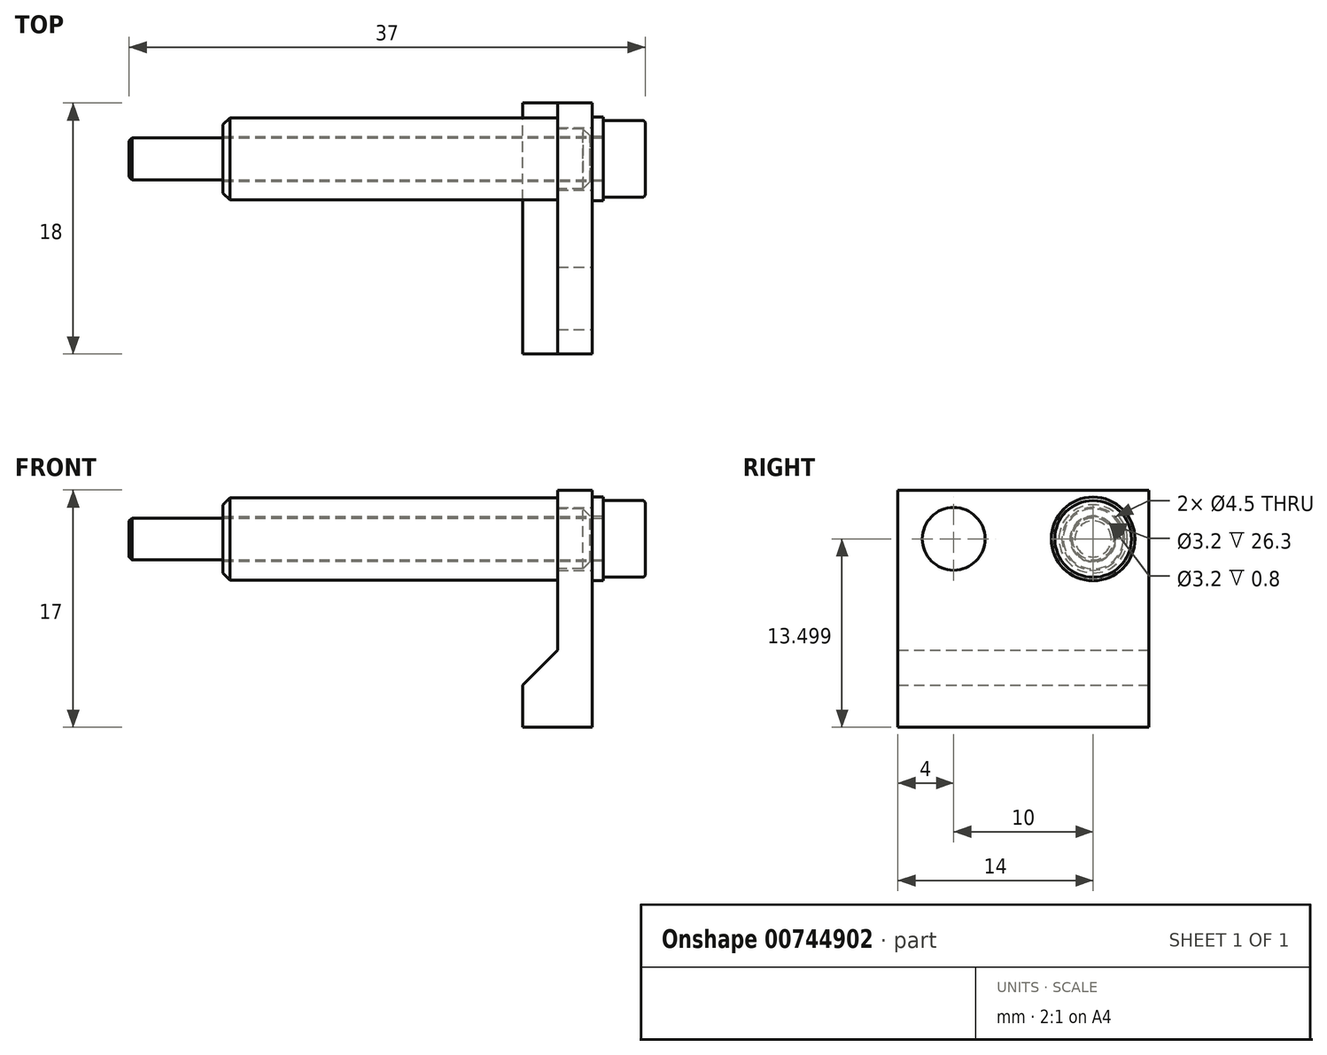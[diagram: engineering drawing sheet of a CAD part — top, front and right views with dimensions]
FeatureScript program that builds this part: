
annotation { "Feature Type Name" : "Feature", "Feature Type Description" : "" }
export const myFeature = defineFeature(function(context is Context, id is Id, definition is map)
    precondition{}
    {
        {
            var Q0;
            Q0=qCreatedBy(makeId("Front.planeOp"),FACE);
            var sketch = newSketch(context, id + "F0", { "sketchPlane" : qUnion([Q0])});
            skLineSegment(sketch, "E0", {"start": v(7.36, -9.32) * mm, "end": v(7.36, -5.59) * mm, "construction": true});
            skLineSegment(sketch, "E1", {"start": v(7.36, -5.59) * mm, "end": v(8.08, -5.59) * mm, "construction": true});
            skLineSegment(sketch, "E2", {"start": v(7.36, -9.32) * mm, "end": v(0, -9.32) * mm, "construction": true});
            skLineSegment(sketch, "E3", {"start": v(8.08, 0) * mm, "end": v(0, 0) * mm, "construction": true});
            skLineSegment(sketch, "E4", {"start": v(10.6, -3.06) * mm, "end": v(10.6, -2.53) * mm, "construction": true});
            skLineSegment(sketch, "E5", {"start": v(8.08, -5.59) * mm, "end": v(8.78, -4.88) * mm, "construction": true});
            skLineSegment(sketch, "E6", {"start": v(10.6, -2.53) * mm, "end": v(8.08, 0) * mm, "construction": true});
            skLineSegment(sketch, "E7", {"start": v(8.08, 0) * mm, "end": v(8.08, -5.59) * mm, "construction": true});
            skLineSegment(sketch, "E8", {"start": v(9.5, -4.17) * mm, "end": v(0, -4.17) * mm, "construction": true});
            skLineSegment(sketch, "E9", {"start": v(9.5, -4.17) * mm, "end": v(9.5, -1.42) * mm, "construction": true});
            skLineSegment(sketch, "E10", {"start": v(9.5, -1.42) * mm, "end": v(0, -1.42) * mm, "construction": true});
            skLineSegment(sketch, "E11", {"start": v(0, 0) * mm, "end": v(0, -1.42) * mm, "construction": true});
            skLineSegment(sketch, "E12", {"start": v(0, -4.17) * mm, "end": v(0, -9.32) * mm, "construction": true});
            skLineSegment(sketch, "E13", {"start": v(0, -4.17) * mm, "end": v(0, -1.42) * mm, "construction": true});
            skLineSegment(sketch, "E14.MirrorCS", {"start": v(-7.36, -5.59) * mm, "end": v(-8.08, -5.59) * mm, "construction": true});
            skLineSegment(sketch, "E15.MirrorCS", {"start": v(-8.08, -5.59) * mm, "end": v(-10.6, -3.06) * mm, "construction": true});
            skLineSegment(sketch, "E16.MirrorCS", {"start": v(-10.6, -3.06) * mm, "end": v(-10.6, -2.53) * mm, "construction": true});
            skLineSegment(sketch, "E17.MirrorCS", {"start": v(-10.6, -2.53) * mm, "end": v(-8.08, 0) * mm, "construction": true});
            skLineSegment(sketch, "E18.MirrorCS", {"start": v(-9.5, -1.42) * mm, "end": v(0, -1.42) * mm, "construction": true});
            skLineSegment(sketch, "E19.MirrorCS", {"start": v(-8.08, 0) * mm, "end": v(0, 0) * mm, "construction": true});
            skLineSegment(sketch, "E20.MirrorCS", {"start": v(-7.36, -9.32) * mm, "end": v(-7.36, -5.59) * mm, "construction": true});
            skLineSegment(sketch, "E21.MirrorCS", {"start": v(-9.5, -4.17) * mm, "end": v(-9.5, -1.42) * mm, "construction": true});
            skLineSegment(sketch, "E22.MirrorCS", {"start": v(-7.36, -9.32) * mm, "end": v(0, -9.32) * mm, "construction": true});
            skLineSegment(sketch, "E23.MirrorCS", {"start": v(-9.5, -4.17) * mm, "end": v(0, -4.17) * mm, "construction": true});
            skLineSegment(sketch, "E24.MirrorCS", {"start": v(-8.08, 0) * mm, "end": v(-8.08, -5.59) * mm, "construction": true});
            skLineSegment(sketch, "E25", {"start": v(8.78, -4.88) * mm, "end": v(10.6, -3.06) * mm});
            skLineSegment(sketch, "E26", {"start": v(10.6, -3.06) * mm, "end": v(11.31, -2.35) * mm});
            skLineSegment(sketch, "E27", {"start": v(8.78, -4.88) * mm, "end": v(8.78, -7.88) * mm});
            skLineSegment(sketch, "E28", {"start": v(8.78, -7.88) * mm, "end": v(13.78, -7.88) * mm});
            skLineSegment(sketch, "E29", {"start": v(13.78, -7.88) * mm, "end": v(13.78, 9.12) * mm});
            skLineSegment(sketch, "E30", {"start": v(11.31, 9.12) * mm, "end": v(11.31, -2.35) * mm});
            skLineSegment(sketch, "E31", {"start": v(13.78, 9.12) * mm, "end": v(11.31, 9.12) * mm});
            skSolve(sketch);
        }
        {
            var Q0;
            Q0 = qSketchRegion(id + "F0", true);
            extrude(context, id + "F1", {"entities" : qUnion([Q0]), "endBound" : BoundingType.SYMMETRIC, "depth" : 18 * mm, "offsetDistance" : 25 * mm});
        }
        {
            var Q0;
            Q0=makeQuery(id+"F1.opExtrude","SWEPT_FACE",FACE,{"disambiguationData":[OSD([sQuery(id+"F0.wireOp",EDGE,"E29")])]});
            var sketch = newSketch(context, id + "F2", { "sketchPlane" : qUnion([Q0])});
            skLineSegment(sketch, "E32", {"start": v(-9, 5.62) * mm, "end": v(-5, 5.62) * mm, "construction": true});
            skLineSegment(sketch, "E33", {"start": v(-5, 5.62) * mm, "end": v(5, 5.62) * mm, "construction": true});
            skLineSegment(sketch, "E34", {"start": v(5, 5.62) * mm, "end": v(9, 5.62) * mm, "construction": true});
            skSolve(sketch);
        }
        {
            var Q0;
            Q0=sQuery(id+"F2.wireOp",VERTEX,"E33.start");
            var Q1;
            Q1=sQuery(id+"F2.wireOp",VERTEX,"E34.start");
            var Q2;
            Q2=makeQuery(id+"F1.opExtrude","SWEPT_BODY",BODY,{"disambiguationData":[OSD([sQuery(id+"F0.wireOp",EDGE,"E25"),sQuery(id+"F0.wireOp",EDGE,"E26"),sQuery(id+"F0.wireOp",EDGE,"E27"),sQuery(id+"F0.wireOp",EDGE,"E28"),sQuery(id+"F0.wireOp",EDGE,"E29"),sQuery(id+"F0.wireOp",EDGE,"jxwox8Iy-gYFC-VK8o-ptvJ-4F3VnWy338mb"),sQuery(id+"F0.wireOp",EDGE,"mAjDmbwP-u3rq-lV9H-9kcG-bIBsuvSuJTE3"),sQuery(id+"F0.wireOp",EDGE,"juroiCpw-intV-WaKl-nkkL-CXtJp0xfCT75"),sQuery(id+"F0.wireOp",EDGE,"E30")])]});
            hole(context, id + "F3", {"style" : HoleStyle.SIMPLE, "endStyle" : HoleEndStyle.THROUGH, "holeDiameter" : 4.5 * mm, "majorDiameter" : 5 * mm, "isTappedThrough" : true, "tappedDepth" : 6 * mm, "tapClearance" : 3, "startFromSketch" : true, "locations" : qUnion([Q0, Q1]), "scope" : qUnion([Q2])});
        }
        {
            var Q0;
            Q0=makeQuery(id+"F1.opExtrude","SWEPT_FACE",FACE,{"disambiguationData":[OSD([sQuery(id+"F0.wireOp",EDGE,"E30")])]});
            var sketch = newSketch(context, id + "F4", { "sketchPlane" : qUnion([Q0])});
            skCircle(sketch, "E35", {"center": v(-5, 5.62) * mm, "radius": 2.95 * mm});
            skSolve(sketch);
        }
        {
            var Q0;
            Q0 = qSketchRegion(id + "F4", true);
            extrude(context, id + "F5", {"entities" : qUnion([Q0]), "depth" : 24 * mm, "offsetDistance" : 25 * mm});
        }
        {
            var Q0;
            Q0=makeQuery(id+"F5.opExtrude","CAP_FACE",FACE,{"disambiguationData":[OSD([sQuery(id+"F4.wireOp",EDGE,"E35")])],"isStart":true});
            var sketch = newSketch(context, id + "F6", { "sketchPlane" : qUnion([Q0])});
            skCircle(sketch, "E36", {"center": v(5, 5.62) * mm, "radius": 2.15 * mm});
            skSolve(sketch);
        }
        {
            var Q0;
            Q0 = qSketchRegion(id + "F6", true);
            extrude(context, id + "F7", {"entities" : qUnion([Q0]), "operationType" : NewBodyOperationType.ADD, "depth" : 2.3 * mm, "offsetDistance" : 25 * mm});
        }
        {
            var Q0;
            Q0=makeQuery(id+"F7.opExtrude","CAP_EDGE",EDGE,{"disambiguationData":[OSD([sQuery(id+"F6.wireOp",EDGE,"E36")])],"isStart":false});
            chamfer(context, id + "F8", {"entities" : qUnion([Q0]), "width" : 0.5 * mm, "tangentPropagation" : true});
        }
        {
            var Q0;
            Q0=makeQuery(id+"F5.opExtrude","CAP_EDGE",EDGE,{"disambiguationData":[OSD([sQuery(id+"F4.wireOp",EDGE,"E35")])],"isStart":false});
            chamfer(context, id + "F9", {"entities" : qUnion([Q0]), "width" : 0.5 * mm, "tangentPropagation" : true});
        }
        {
            var Q0;
            Q0=makeQuery(id+"F7.opExtrude","CAP_FACE",FACE,{"disambiguationData":[OSD([sQuery(id+"F6.wireOp",EDGE,"E36")])],"isStart":false});
            var sketch = newSketch(context, id + "F10", { "sketchPlane" : qUnion([Q0])});
            skPoint(sketch, "E37", {"position": v(5, 5.62) * mm});
            skSolve(sketch);
        }
        {
            var Q0;
            Q0=sQuery(id+"F10.wireOp",VERTEX,"E37");
            var Q1;
            Q1=makeQuery(id+"F5.opExtrude","SWEPT_BODY",BODY,{"disambiguationData":[OSD([sQuery(id+"F4.wireOp",EDGE,"E35")])]});
            hole(context, id + "F11", {"style" : HoleStyle.SIMPLE, "endStyle" : HoleEndStyle.THROUGH, "holeDiameter" : 3.2 * mm, "majorDiameter" : 5 * mm, "isTappedThrough" : true, "tappedDepth" : 6 * mm, "tapClearance" : 3, "startFromSketch" : true, "locations" : qUnion([Q0]), "scope" : qUnion([Q1])});
        }
        {
            var Q0;
            Q0=makeQuery(id+"F1.opExtrude","SWEPT_FACE",FACE,{"disambiguationData":[OSD([sQuery(id+"F0.wireOp",EDGE,"E29")])]});
            var sketch = newSketch(context, id + "F12", { "sketchPlane" : qUnion([Q0])});
            skCircle(sketch, "E38", {"center": v(5, 5.62) * mm, "radius": 1.6 * mm});
            skCircle(sketch, "E39", {"center": v(5, 5.62) * mm, "radius": 3 * mm});
            skSolve(sketch);
        }
        {
            var Q0;
            Q0 = qSketchRegion(id + "F12", true);
            extrude(context, id + "F13", {"entities" : qUnion([Q0]), "depth" : 0.8 * mm, "offsetDistance" : 25 * mm});
        }
        {
            var Q0;
            Q0=makeQuery(id+"F13.opExtrude","CAP_FACE",FACE,{"disambiguationData":[OSD([sQuery(id+"F12.wireOp",EDGE,"E38"),sQuery(id+"F12.wireOp",EDGE,"E39")])],"isStart":false});
            var sketch = newSketch(context, id + "F14", { "sketchPlane" : qUnion([Q0])});
            skCircle(sketch, "E40", {"center": v(5, 5.62) * mm, "radius": 1.5 * mm});
            skSolve(sketch);
        }
        {
            var Q0;
            Q0 = qSketchRegion(id + "F14", true);
            extrude(context, id + "F15", {"entities" : qUnion([Q0]), "oppositeDirection" : true, "depth" : 34 * mm, "offsetDistance" : 25 * mm});
        }
        {
            var Q0;
            Q0=makeQuery(id+"F15.opExtrude","CAP_FACE",FACE,{"disambiguationData":[OSD([sQuery(id+"F14.wireOp",EDGE,"E40")])],"isStart":true});
            var sketch = newSketch(context, id + "F16", { "sketchPlane" : qUnion([Q0])});
            skCircle(sketch, "E41", {"center": v(5, 5.62) * mm, "radius": 2.75 * mm});
            skSolve(sketch);
        }
        {
            var Q0;
            Q0 = qSketchRegion(id + "F16", true);
            extrude(context, id + "F17", {"entities" : qUnion([Q0]), "operationType" : NewBodyOperationType.ADD, "depth" : 3 * mm, "offsetDistance" : 25 * mm});
        }
        {
            var Q0;
            Q0=makeQuery(id+"F17.opExtrude","CAP_EDGE",EDGE,{"disambiguationData":[OSD([sQuery(id+"F16.wireOp",EDGE,"E41")])],"isStart":false});
            var Q1;
            Q1=makeQuery(id+"F15.opExtrude","CAP_EDGE",EDGE,{"disambiguationData":[OSD([sQuery(id+"F14.wireOp",EDGE,"E40")])],"isStart":true});
            fillet(context, id + "F18", {"entities" : qUnion([Q0, Q1]), "radius" : 0.2 * mm, "tangentPropagation" : true, "allowEdgeOverflow" : false});
        }
        {
            var Q0;
            Q0=makeQuery(id+"F15.opExtrude","CAP_EDGE",EDGE,{"disambiguationData":[OSD([sQuery(id+"F14.wireOp",EDGE,"E40")])],"isStart":false});
            chamfer(context, id + "F19", {"entities" : qUnion([Q0]), "width" : 0.2 * mm, "tangentPropagation" : true});
        }
    });
